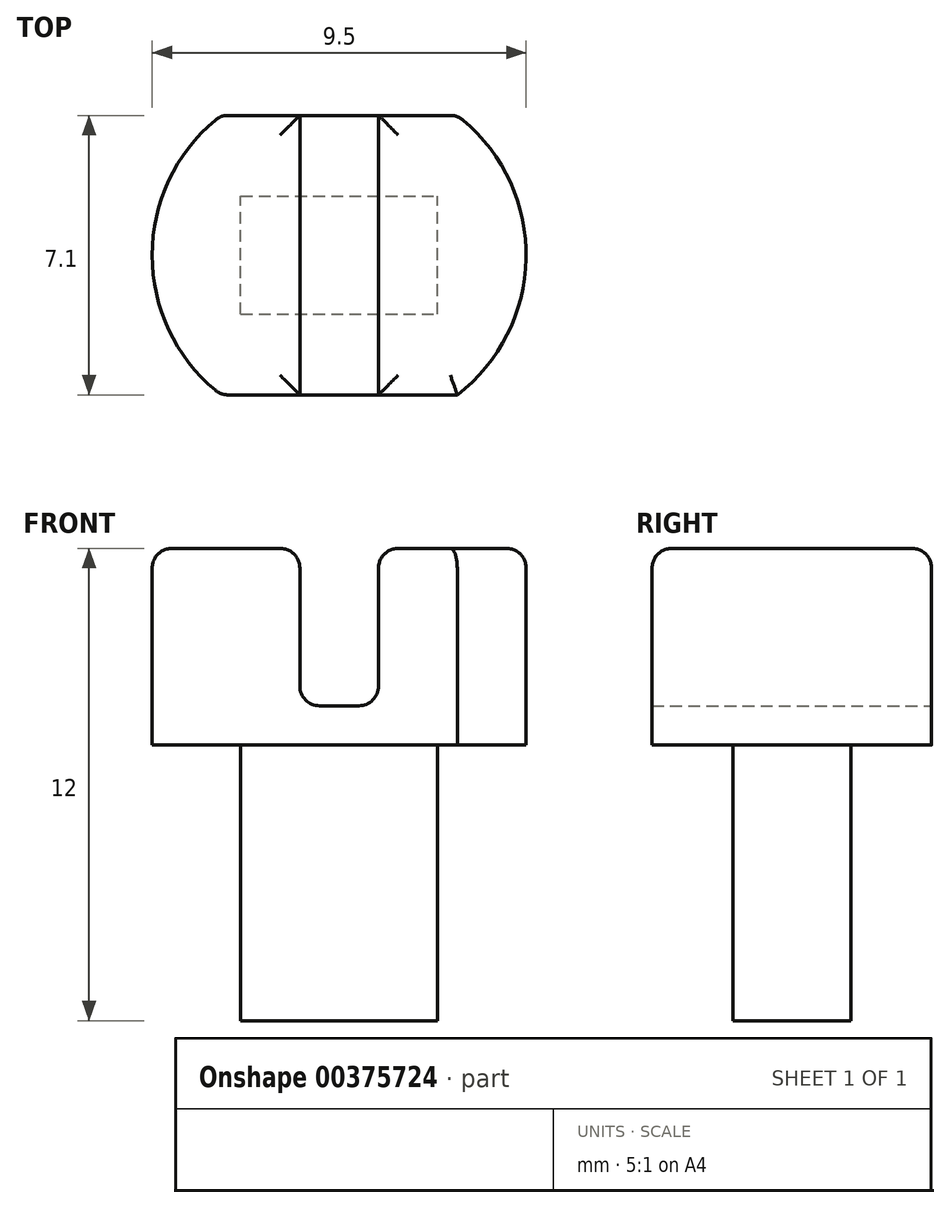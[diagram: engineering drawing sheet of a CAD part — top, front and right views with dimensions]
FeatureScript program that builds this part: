
annotation { "Feature Type Name" : "Feature", "Feature Type Description" : "" }
export const myFeature = defineFeature(function(context is Context, id is Id, definition is map)
    precondition{}
    {
        {
            var Q0;
            Q0=qCreatedBy(makeId("Top.planeOp"),FACE);
            var sketch = newSketch(context, id + "F0", { "sketchPlane" : qUnion([Q0])});
            skLineSegment(sketch, "E0", {"start": v(-6, 7.1) * mm, "end": v(0, 7.1) * mm});
            skLineSegment(sketch, "E1", {"start": v(0, 0) * mm, "end": v(-6, 0) * mm});
            skArc(sketch, "E2", {"start": v(0, 0) * mm, "mid": v(1.75, 3.55) * mm, "end": v(0, 7.1) * mm});
            skArc(sketch, "E3", {"start": v(-6, 7.1) * mm, "mid": v(-7.75, 3.55) * mm, "end": v(-6, 0) * mm});
            skLineSegment(sketch, "E4", {"start": v(-3, 7.1) * mm, "end": v(-3, 0) * mm});
            skLineSegment(sketch, "E5", {"start": v(-3.27, 3.55) * mm, "end": v(-3, 3.55) * mm});
            skLineSegment(sketch, "E6", {"start": v(-3, 3.55) * mm, "end": v(-2.73, 3.55) * mm});
            skLineSegment(sketch, "E7", {"start": v(-6, 0) * mm, "end": v(-6, 7.1) * mm});
            skLineSegment(sketch, "E8", {"start": v(0, 0) * mm, "end": v(0, 7.1) * mm});
            skSolve(sketch);
        }
        {
            var Q0;
            Q0 = qSketchRegion(id + "F0", true);
            extrude(context, id + "F1", {"entities" : qUnion([Q0]), "depth" : 5 * mm});
        }
        {
            var Q0;
            Q0=makeQuery(id+"F1.opExtrude","CAP_FACE",FACE,{"disambiguationData":[OSD([sQuery(id+"F0.wireOp",EDGE,"E0"),sQuery(id+"F0.wireOp",EDGE,"E1"),sQuery(id+"F0.wireOp",EDGE,"E2"),sQuery(id+"F0.wireOp",EDGE,"E3")])],"isStart":false});
            var sketch = newSketch(context, id + "F2", { "sketchPlane" : qUnion([Q0])});
            skLineSegment(sketch, "E9", {"start": v(-3, 7.1) * mm, "end": v(-3, 0) * mm});
            skLineSegment(sketch, "E10", {"start": v(-4, 7.1) * mm, "end": v(-4, 0) * mm});
            skLineSegment(sketch, "E11", {"start": v(-2, 0) * mm, "end": v(-2, 7.1) * mm});
            skSolve(sketch);
        }
        {
            var Q0;
            {var subQ0=sQuery(id+"F2.wireOp",EDGE,"E9");Q0=makeQuery(id+"F2.imprint","IMPRINT",FACE,{"disambiguationData":[TD([[makeQuery(id+"F2.imprint","IMPRINT",EDGE,{"derivedFrom":subQ0}),-1.0]])]});}
            var Q1;
            {var subQ0=sQuery(id+"F2.wireOp",EDGE,"E9");Q1=makeQuery(id+"F2.imprint","IMPRINT",FACE,{"disambiguationData":[TD([[makeQuery(id+"F2.imprint","IMPRINT",EDGE,{"derivedFrom":subQ0}),1.0]])]});}
            extrude(context, id + "F3", {"entities" : qUnion([Q0, Q1]), "operationType" : NewBodyOperationType.REMOVE, "oppositeDirection" : true, "depth" : 4 * mm});
        }
        {
            var Q0;
            {var subQ0=sQuery(id+"F0.wireOp",EDGE,"E0");var subQ1=sQuery(id+"F0.wireOp",EDGE,"E3");var subQ2=sQuery(id+"F0.wireOp",EDGE,"E1");Q0=makeQuery(id+"F3.boolean.opBoolean","SPLIT",FACE,{"disambiguationData":[TD([makeQuery(id+"F1.opExtrude","SWEPT_FACE",FACE,{"disambiguationData":[OSD([subQ1])]})])],"derivedFrom":makeQuery(id+"F1.opExtrude","CAP_FACE",FACE,{"disambiguationData":[OSD([subQ0,subQ2,sQuery(id+"F0.wireOp",EDGE,"E2"),subQ1])],"isStart":false})});}
            var Q1;
            {var subQ0=sQuery(id+"F0.wireOp",EDGE,"E0");var subQ1=sQuery(id+"F0.wireOp",EDGE,"E1");var subQ2=sQuery(id+"F0.wireOp",EDGE,"E2");Q1=makeQuery(id+"F3.boolean.opBoolean","SPLIT",FACE,{"disambiguationData":[TD([makeQuery(id+"F1.opExtrude","SWEPT_FACE",FACE,{"disambiguationData":[OSD([subQ2])]})])],"derivedFrom":makeQuery(id+"F1.opExtrude","CAP_FACE",FACE,{"disambiguationData":[OSD([subQ0,subQ1,subQ2,sQuery(id+"F0.wireOp",EDGE,"E3")])],"isStart":false})});}
            var Q2;
            Q2=makeQuery(id+"F3.boolean.opBoolean","COPY",EDGE,{"derivedFrom":makeQuery(id+"F3.opExtrude","CAP_EDGE",EDGE,{"disambiguationData":[OSD([sQuery(id+"F2.wireOp",EDGE,"E10")])],"isStart":false})});
            var Q3;
            Q3=makeQuery(id+"F3.boolean.opBoolean","COPY",EDGE,{"derivedFrom":makeQuery(id+"F3.opExtrude","CAP_EDGE",EDGE,{"disambiguationData":[OSD([sQuery(id+"F2.wireOp",EDGE,"E11")])],"isStart":false})});
            var Q4;
            Q4=makeQuery(id+"F3.boolean.opBoolean","COPY",EDGE,{"derivedFrom":makeQuery(id+"F3.opExtrude","CAP_EDGE",EDGE,{"disambiguationData":[OSD([sQuery(id+"F0.wireOp",EDGE,"E1")])],"isStart":false})});
            var Q5;
            Q5=makeQuery(id+"F3.boolean.opBoolean","COPY",EDGE,{"derivedFrom":makeQuery(id+"F3.opExtrude","CAP_EDGE",EDGE,{"disambiguationData":[OSD([sQuery(id+"F0.wireOp",EDGE,"E0")])],"isStart":false})});
            var Q6;
            Q6=makeQuery(id+"F1.opExtrude","SWEPT_EDGE",EDGE,{"disambiguationData":[OSD([sQuery(id+"F0.wireOp",EDGE,"E0"),sQuery(id+"F0.wireOp",EDGE,"E2")])]});
            var Q7;
            Q7=makeQuery(id+"F1.opExtrude","SWEPT_EDGE",EDGE,{"disambiguationData":[OSD([sQuery(id+"F0.wireOp",EDGE,"E0"),sQuery(id+"F0.wireOp",EDGE,"E3")])]});
            var Q8;
            Q8=makeQuery(id+"F1.opExtrude","SWEPT_EDGE",EDGE,{"disambiguationData":[OSD([sQuery(id+"F0.wireOp",EDGE,"E1"),sQuery(id+"F0.wireOp",EDGE,"E3")])]});
            fillet(context, id + "F4", {"entities" : qUnion([Q0, Q1, Q2, Q3, Q4, Q5, Q6, Q7, Q8]), "radius" : 0.5 * mm, "tangentPropagation" : true, "allowEdgeOverflow" : false});
        }
        {
            var Q0;
            Q0=makeQuery(id+"F1.opExtrude","CAP_FACE",FACE,{"disambiguationData":[OSD([sQuery(id+"F0.wireOp",EDGE,"E0"),sQuery(id+"F0.wireOp",EDGE,"E1"),sQuery(id+"F0.wireOp",EDGE,"E2"),sQuery(id+"F0.wireOp",EDGE,"E3")])],"isStart":true});
            var sketch = newSketch(context, id + "F5", { "sketchPlane" : qUnion([Q0])});
            skLineSegment(sketch, "E12.bottom", {"start": v(-5.5, -2.05) * mm, "end": v(-0.5, -2.05) * mm});
            skLineSegment(sketch, "E12.top", {"start": v(-5.5, -5.05) * mm, "end": v(-0.5, -5.05) * mm});
            skLineSegment(sketch, "E12.left", {"start": v(-5.5, -2.05) * mm, "end": v(-5.5, -5.05) * mm});
            skLineSegment(sketch, "E12.right", {"start": v(-0.5, -2.05) * mm, "end": v(-0.5, -5.05) * mm});
            skLineSegment(sketch, "E13", {"start": v(-3, 0) * mm, "end": v(-3, -7.1) * mm});
            skLineSegment(sketch, "E14", {"start": v(-5.5, -3.55) * mm, "end": v(-0.5, -3.55) * mm});
            skSolve(sketch);
        }
        {
            var Q0;
            {var subQ0=sQuery(id+"F5.wireOp",EDGE,"E12.left");var subQ1=sQuery(id+"F5.wireOp",EDGE,"E12.bottom");var subQ2=makeQuery(id+"F5.imprint","INTERSECT",VERTEX,{"derivedFrom":[subQ1,subQ0]});Q0=makeQuery(id+"F5.imprint","IMPRINT",FACE,{"disambiguationData":[TD([[makeQuery(id+"F5.imprint","IMPRINT",EDGE,{"disambiguationData":[TD([[subQ2,-1.0]])],"derivedFrom":subQ1}),-1.0]])]});}
            var Q1;
            {var subQ0=sQuery(id+"F5.wireOp",EDGE,"E12.right");var subQ1=sQuery(id+"F5.wireOp",EDGE,"E12.bottom");var subQ2=makeQuery(id+"F5.imprint","INTERSECT",VERTEX,{"derivedFrom":[subQ1,subQ0]});Q1=makeQuery(id+"F5.imprint","IMPRINT",FACE,{"disambiguationData":[TD([[makeQuery(id+"F5.imprint","IMPRINT",EDGE,{"disambiguationData":[TD([[subQ2,1.0]])],"derivedFrom":subQ1}),-1.0]])]});}
            var Q2;
            {var subQ0=sQuery(id+"F5.wireOp",EDGE,"E12.right");var subQ1=sQuery(id+"F5.wireOp",EDGE,"E12.top");var subQ2=makeQuery(id+"F5.imprint","INTERSECT",VERTEX,{"derivedFrom":[subQ1,subQ0]});Q2=makeQuery(id+"F5.imprint","IMPRINT",FACE,{"disambiguationData":[TD([[makeQuery(id+"F5.imprint","IMPRINT",EDGE,{"disambiguationData":[TD([[subQ2,1.0]])],"derivedFrom":subQ1}),1.0]])]});}
            var Q3;
            {var subQ0=sQuery(id+"F5.wireOp",EDGE,"E12.left");var subQ1=sQuery(id+"F5.wireOp",EDGE,"E12.top");var subQ2=makeQuery(id+"F5.imprint","INTERSECT",VERTEX,{"derivedFrom":[subQ1,subQ0]});Q3=makeQuery(id+"F5.imprint","IMPRINT",FACE,{"disambiguationData":[TD([[makeQuery(id+"F5.imprint","IMPRINT",EDGE,{"disambiguationData":[TD([[subQ2,-1.0]])],"derivedFrom":subQ1}),1.0]])]});}
            extrude(context, id + "F6", {"entities" : qUnion([Q0, Q1, Q2, Q3]), "operationType" : NewBodyOperationType.ADD, "depth" : 7 * mm});
        }
    });
